# Revit family: 720126
name_source: partatom
category: Sanitärinstallationen
revit_build: Autodesk Revit 2014 (Build: 20130308_1515(x64)
units: mm (PartAtom-declared; Revit-internal decimal feet)

## types (1)
- 720126
    Abwasserrohrverbindung = Nein
    Baugruppenkennzeichen = D2010510
    Behindertengerecht / ADA Compliant = Ja
    Familie von / Family made By = http://bytesandbuilding.de
    HW-Verbindung = Nein
    Hersteller = Duravit
    KW-Verbindung = Nein
    LEED Credit = 0
    Lüftungsverbindung = Nein
    Material Chrom = Stahl, verchromt
    Material Keramik = Duravit Keramik
    Modell = 720126
    Modellbezeichnung / Modeldescription = Duschwanne Starck Slimline / Shower tray Starck Slimline
Ovalwanne Starck 1900x900mm Weiss
Ovalwanne Starck 1900x900mm Weiss / Oval bathtub Starck 1900x900mm
    Produktseite / Product URL = http://www.pro.duravit.com
    URL = http://www.duravit.de

## geometry (parser evidence)
native form markers: Blend x4
no freeform markers — native parametric forms only
